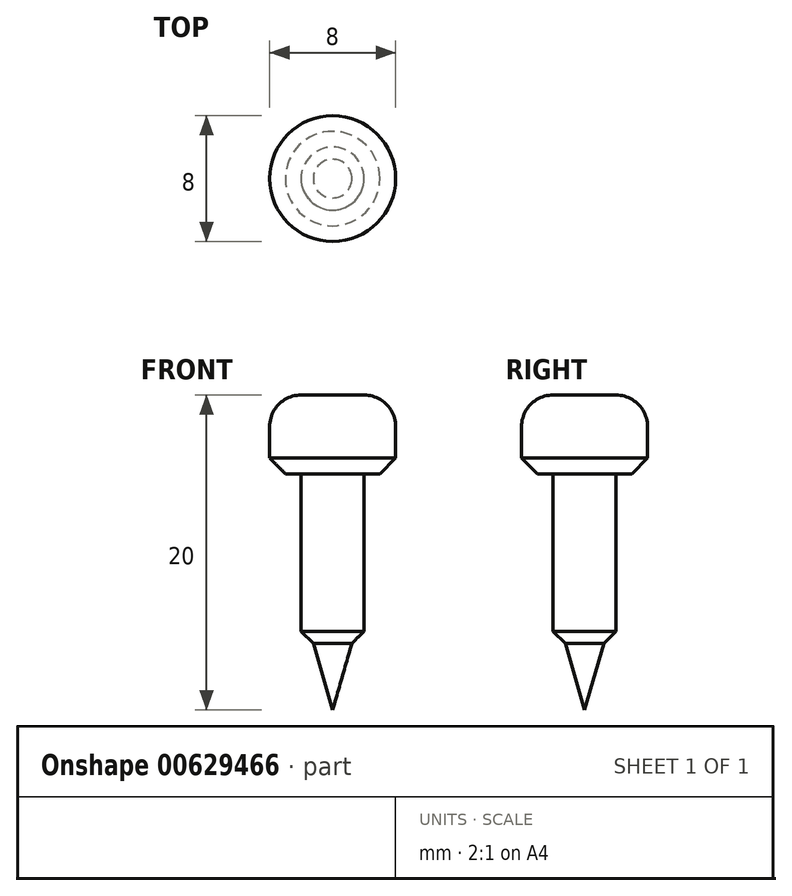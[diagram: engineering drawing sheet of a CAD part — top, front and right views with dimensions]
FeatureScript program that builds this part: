
annotation { "Feature Type Name" : "Feature", "Feature Type Description" : "" }
export const myFeature = defineFeature(function(context is Context, id is Id, definition is map)
    precondition{}
    {
        {
            var Q0;
            Q0=qCreatedBy(makeId("Right.planeOp"),FACE);
            var sketch = newSketch(context, id + "F0", { "sketchPlane" : qUnion([Q0])});
            skLineSegment(sketch, "E0", {"start": v(0, 0) * mm, "end": v(-2, 0) * mm});
            skLineSegment(sketch, "E1", {"start": v(-2, -16) * mm, "end": v(-1.16, -16) * mm});
            skLineSegment(sketch, "E2", {"start": v(-1.16, -16) * mm, "end": v(0, -20) * mm});
            skLineSegment(sketch, "E3", {"start": v(0, -20) * mm, "end": v(0, 0) * mm});
            skLineSegment(sketch, "E4", {"start": v(-2, 0) * mm, "end": v(-2, -16) * mm});
            skLineSegment(sketch, "E5.bottom", {"start": v(-2, 0) * mm, "end": v(-4, 0) * mm});
            skLineSegment(sketch, "E5.top", {"start": v(-2, -5) * mm, "end": v(-4, -5) * mm});
            skLineSegment(sketch, "E5.left", {"start": v(-2, 0) * mm, "end": v(-2, -5) * mm});
            skLineSegment(sketch, "E5.right", {"start": v(-4, 0) * mm, "end": v(-4, -5) * mm});
            skSolve(sketch);
        }
        {
            var Q0;
            Q0 = qSketchRegion(id + "F0", true);
            var Q1;
            Q1=sQuery(id+"F0.wireOp",EDGE,"E3");
            revolve(context, id + "F1", {"entities" : qUnion([Q0]), "axis" : qUnion([Q1]), "revolveType" : RevolveType.FULL});
        }
        {
            var Q0;
            Q0=makeQuery(id+"F1.opRevolve","SWEPT_EDGE",EDGE,{"disambiguationData":[OSD([sQuery(id+"F0.wireOp",EDGE,"E5.bottom"),sQuery(id+"F0.wireOp",EDGE,"E5.right")])]});
            fillet(context, id + "F2", {"entities" : qUnion([Q0]), "radius" : 2 * mm, "tangentPropagation" : true, "allowEdgeOverflow" : false});
        }
        {
            var Q0;
            Q0=makeQuery(id+"F1.opRevolve","SWEPT_EDGE",EDGE,{"disambiguationData":[OSD([sQuery(id+"F0.wireOp",EDGE,"E1"),sQuery(id+"F0.wireOp",EDGE,"E4")])]});
            var Q1;
            Q1=makeQuery(id+"F1.opRevolve","SWEPT_EDGE",EDGE,{"disambiguationData":[OSD([sQuery(id+"F0.wireOp",EDGE,"E5.top"),sQuery(id+"F0.wireOp",EDGE,"E5.right")])]});
            chamfer(context, id + "F3", {"entities" : qUnion([Q0, Q1]), "width" : 1 * mm, "tangentPropagation" : true});
        }
    });
